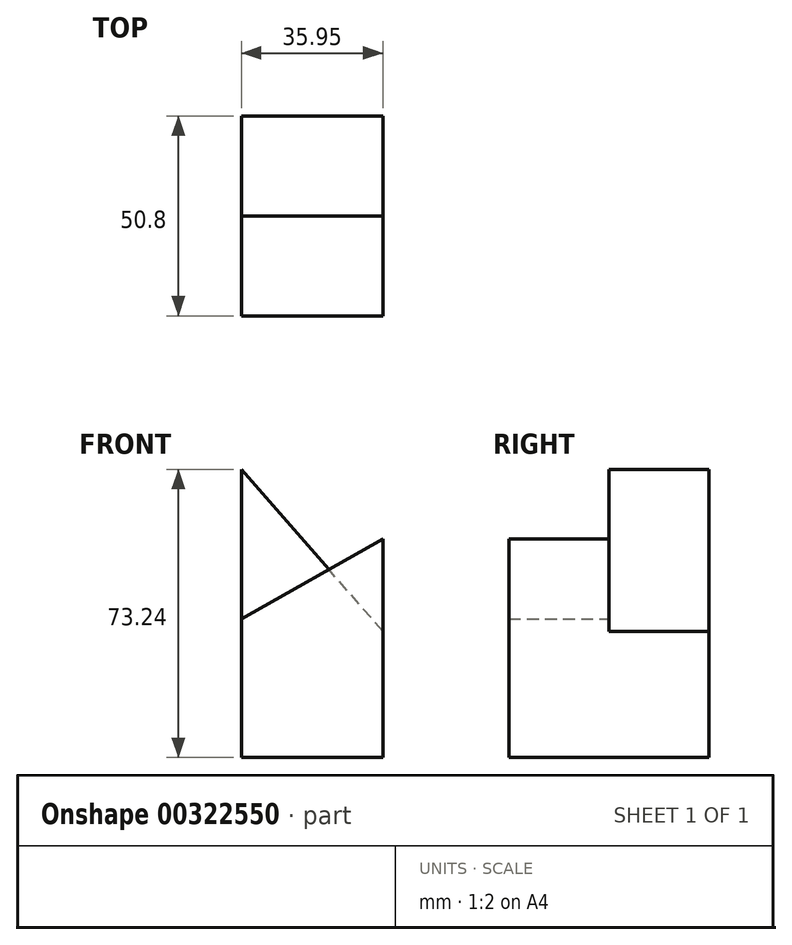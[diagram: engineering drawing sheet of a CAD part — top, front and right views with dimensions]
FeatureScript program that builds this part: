
annotation { "Feature Type Name" : "Feature", "Feature Type Description" : "" }
export const myFeature = defineFeature(function(context is Context, id is Id, definition is map)
    precondition{}
    {
        {
            var Q0;
            Q0=qCreatedBy(makeId("Front.planeOp"),FACE);
            var sketch = newSketch(context, id + "F0", { "sketchPlane" : qUnion([Q0])});
            skLineSegment(sketch, "E0", {"start": v(35.95, 55.6) * mm, "end": v(35.95, 0) * mm});
            skLineSegment(sketch, "E1", {"start": v(35.95, 0) * mm, "end": v(0, 0) * mm});
            skLineSegment(sketch, "E2", {"start": v(0, 0) * mm, "end": v(0, 35.27) * mm});
            skLineSegment(sketch, "E3", {"start": v(0, 35.27) * mm, "end": v(35.95, 55.6) * mm});
            skSolve(sketch);
        }
        {
            var Q0;
            Q0=makeQuery(id+"F0.imprint","IMPRINT",FACE,{"disambiguationData":[TD([[makeQuery(id+"F0.imprint","IMPRINT",EDGE,{"derivedFrom":sQuery(id+"F0.wireOp",EDGE,"E0")}),-1.0]])]});
            extrude(context, id + "F1", {"entities" : qUnion([Q0]), "depth" : 25.4 * mm});
        }
        {
            var Q0;
            Q0=qCreatedBy(makeId("Front.planeOp"),FACE);
            var sketch = newSketch(context, id + "F2", { "sketchPlane" : qUnion([Q0])});
            skLineSegment(sketch, "E4", {"start": v(0, 0) * mm, "end": v(35.94, 0) * mm});
            skLineSegment(sketch, "E5", {"start": v(35.94, 0) * mm, "end": v(35.94, 32.1) * mm});
            skLineSegment(sketch, "E6", {"start": v(35.94, 32.1) * mm, "end": v(0, 73.24) * mm});
            skLineSegment(sketch, "E7", {"start": v(0, 73.24) * mm, "end": v(0, 0) * mm});
            skSolve(sketch);
        }
        {
            var Q0;
            Q0=makeQuery(id+"F2.imprint","IMPRINT",FACE,{"disambiguationData":[TD([[makeQuery(id+"F2.imprint","IMPRINT",EDGE,{"derivedFrom":sQuery(id+"F2.wireOp",EDGE,"E4")}),1.0]])]});
            extrude(context, id + "F3", {"entities" : qUnion([Q0]), "operationType" : NewBodyOperationType.ADD, "oppositeDirection" : true, "depth" : 25.4 * mm});
        }
    });
